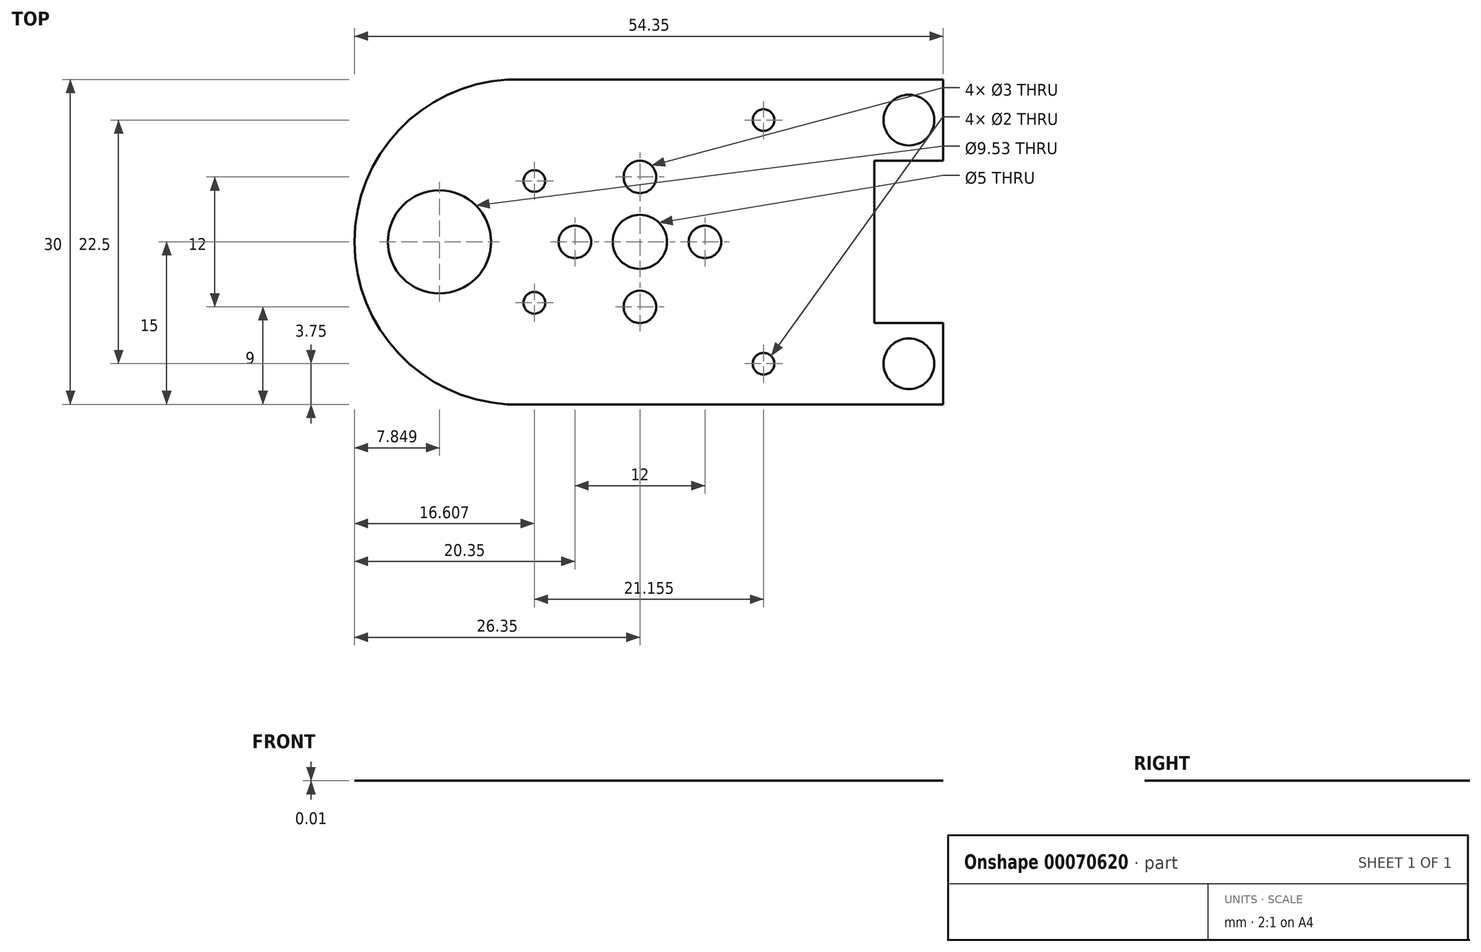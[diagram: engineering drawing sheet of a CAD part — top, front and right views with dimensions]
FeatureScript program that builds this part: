
annotation { "Feature Type Name" : "Feature", "Feature Type Description" : "" }
export const myFeature = defineFeature(function(context is Context, id is Id, definition is map)
    precondition{}
    {
        {
            var Q0;
            Q0=qCreatedBy(makeId("Top.planeOp"),FACE);
            var sketch = newSketch(context, id + "F0", { "sketchPlane" : qUnion([Q0])});
            skCircle(sketch, "E0.3.0", {"center": v(-6, 0) * mm, "radius": 1.5 * mm});
            skCircle(sketch, "E1", {"center": v(0, 0) * mm, "radius": 2.5 * mm});
            skCircle(sketch, "E0.1.0", {"center": v(-6, 0) * mm, "radius": 1.5 * mm});
            skLineSegment(sketch, "E2", {"start": v(-2.5, 0) * mm, "end": v(-9.5, 0) * mm});
            skLineSegment(sketch, "E3.bottom", {"start": v(-12.25, 15) * mm, "end": v(28, 15) * mm});
            skLineSegment(sketch, "E3.top", {"start": v(-12.25, -15) * mm, "end": v(28, -15) * mm});
            skLineSegment(sketch, "E3.right", {"start": v(28, 15) * mm, "end": v(28, -15) * mm});
            skCircle(sketch, "E4.1.0", {"center": v(0, -6) * mm, "radius": 1.5 * mm});
            skCircle(sketch, "E4.2.0", {"center": v(6, 0) * mm, "radius": 1.5 * mm});
            skCircle(sketch, "E4.3.0", {"center": v(0, 6) * mm, "radius": 1.5 * mm});
            skPoint(sketch, "E5", {"position": v(7.5, 0) * mm});
            skPoint(sketch, "E5.positionSnap0", {"position": v(10.05, 0) * mm});
            skLineSegment(sketch, "E6.bottom", {"start": v(21.65, 7.5) * mm, "end": v(28, 7.5) * mm});
            skLineSegment(sketch, "E6.top", {"start": v(21.65, -7.5) * mm, "end": v(28, -7.5) * mm});
            skLineSegment(sketch, "E6.left", {"start": v(21.65, 7.5) * mm, "end": v(21.65, -7.5) * mm});
            skLineSegment(sketch, "E6.right", {"start": v(28, 7.5) * mm, "end": v(28, -7.5) * mm});
            skPoint(sketch, "E7", {"position": v(24.83, 11.25) * mm});
            skPoint(sketch, "E8", {"position": v(24.83, -11.25) * mm});
            skPoint(sketch, "E9", {"position": v(0, 11.25) * mm});
            skPoint(sketch, "E10.1.0", {"position": v(-9.74, 5.63) * mm});
            skPoint(sketch, "E10.2.0", {"position": v(-9.74, -5.62) * mm});
            skPoint(sketch, "E10.3.0", {"position": v(0, -11.25) * mm});
            skPoint(sketch, "E10.4.0", {"position": v(9.74, -5.63) * mm});
            skPoint(sketch, "E10.5.0", {"position": v(9.74, 5.62) * mm});
            skLineSegment(sketch, "E11", {"start": v(-25.85, 3.84) * mm, "end": v(-25.85, -3.84) * mm});
            skPoint(sketch, "E12", {"position": v(-26.35, 0) * mm});
            skPoint(sketch, "E13", {"position": v(-25.85, 3.84) * mm});
            skPoint(sketch, "E14", {"position": v(-25.85, -3.84) * mm});
            skPoint(sketch, "E15", {"position": v(-12.25, 15) * mm});
            skPoint(sketch, "E16", {"position": v(-12.25, -15) * mm});
            skArc(sketch, "E17", {"start": v(-12.25, 15) * mm, "mid": v(-26.35, 0) * mm, "end": v(-12.25, -15) * mm});
            skCircle(sketch, "E18", {"center": v(-18.5, 0) * mm, "radius": 4.76 * mm});
            skSolve(sketch);
        }
        {
            var Q0;
            Q0=makeQuery(id+"F0.imprint","IMPRINT",FACE,{"disambiguationData":[TD([[makeQuery(id+"F0.imprint","IMPRINT",EDGE,{"derivedFrom":sQuery(id+"F0.wireOp",EDGE,"E1")}),-1.0]])]});
            var Q1;
            {var subQ2=sQuery(id+"F0.wireOp",EDGE,"E3.bottom");Q1=makeQuery(id+"F0.imprint","IMPRINT",FACE,{"disambiguationData":[TD([[makeQuery(id+"F0.imprint","IMPRINT",EDGE,{"derivedFrom":subQ2}),-1.0]])]});}
            extrude(context, id + "F1", {"entities" : qUnion([Q0, Q1]), "depth" : 1 / 101.6 * mm});
        }
        {
            var Q0;
            Q0=sQuery(id+"F0.wireOp",VERTEX,"E7");
            var Q1;
            Q1=sQuery(id+"F0.wireOp",VERTEX,"E8");
            var Q2;
            Q2=makeQuery(id+"F1.opExtrude","SWEPT_BODY",BODY,{"disambiguationData":[OSD([sQuery(id+"F0.wireOp",EDGE,"E1"),sQuery(id+"F0.wireOp",EDGE,"E0.1.0"),sQuery(id+"F0.wireOp",EDGE,"E3.bottom"),sQuery(id+"F0.wireOp",EDGE,"E3.top"),sQuery(id+"F0.wireOp",EDGE,"E3.right"),sQuery(id+"F0.wireOp",EDGE,"E4.1.0"),sQuery(id+"F0.wireOp",EDGE,"E4.2.0"),sQuery(id+"F0.wireOp",EDGE,"E4.3.0"),sQuery(id+"F0.wireOp",EDGE,"Qfz2i4fl-gXpp-EPbZ-7ioY-sWL0IBWqoAn5"),sQuery(id+"F0.wireOp",EDGE,"E6.bottom"),sQuery(id+"F0.wireOp",EDGE,"E6.top"),sQuery(id+"F0.wireOp",EDGE,"E6.left")])]});
            hole(context, id + "F2", {"style" : HoleStyle.C_SINK, "endStyle" : HoleEndStyle.THROUGH, "oppositeDirection" : true, "holeDiameter" : 2.5 * mm, "cSinkDiameter" : 4.7 * mm, "cSinkAngle" : 90 * degree, "locations" : qUnion([Q0, Q1]), "scope" : qUnion([Q2]), "isTappedThrough" : true});
        }
        {
            var Q0;
            Q0=makeQuery(id+"F1.opExtrude","SWEPT_FACE",FACE,{"disambiguationData":[OSD([sQuery(id+"F0.wireOp",EDGE,"E6.left")])]});
            var sketch = newSketch(context, id + "F3", { "sketchPlane" : qUnion([Q0])});
            skPoint(sketch, "E19", {"position": v(0, 3.18) * mm});
            skSolve(sketch);
        }
        {
            var Q0;
            Q0=sQuery(id+"F3.wireOp",VERTEX,"E19");
            var Q1;
            Q1=makeQuery(id+"F1.opExtrude","SWEPT_BODY",BODY,{"disambiguationData":[OSD([sQuery(id+"F0.wireOp",EDGE,"E1"),sQuery(id+"F0.wireOp",EDGE,"E0.1.0"),sQuery(id+"F0.wireOp",EDGE,"E3.bottom"),sQuery(id+"F0.wireOp",EDGE,"E3.top"),sQuery(id+"F0.wireOp",EDGE,"E3.right"),sQuery(id+"F0.wireOp",EDGE,"E4.1.0"),sQuery(id+"F0.wireOp",EDGE,"E4.2.0"),sQuery(id+"F0.wireOp",EDGE,"E4.3.0"),sQuery(id+"F0.wireOp",EDGE,"Qfz2i4fl-gXpp-EPbZ-7ioY-sWL0IBWqoAn5"),sQuery(id+"F0.wireOp",EDGE,"E6.bottom"),sQuery(id+"F0.wireOp",EDGE,"E6.top"),sQuery(id+"F0.wireOp",EDGE,"E6.left")])]});
            hole(context, id + "F4", {"style" : HoleStyle.SIMPLE, "endStyle" : HoleEndStyle.BLIND, "holeDiameter" : 2.05 * mm, "holeDepth" : 12.5 * mm, "locations" : qUnion([Q0]), "scope" : qUnion([Q1])});
        }
        {
            var Q0;
            Q0=sQuery(id+"F0.wireOp",VERTEX,"E10.2.0");
            var Q1;
            Q1=sQuery(id+"F0.wireOp",VERTEX,"E10.1.0");
            var Q2;
            Q2=makeQuery(id+"F1.opExtrude","SWEPT_BODY",BODY,{"disambiguationData":[OSD([sQuery(id+"F0.wireOp",EDGE,"E1"),sQuery(id+"F0.wireOp",EDGE,"E0.1.0"),sQuery(id+"F0.wireOp",EDGE,"E3.bottom"),sQuery(id+"F0.wireOp",EDGE,"E3.top"),sQuery(id+"F0.wireOp",EDGE,"E3.right"),sQuery(id+"F0.wireOp",EDGE,"E4.1.0"),sQuery(id+"F0.wireOp",EDGE,"E4.2.0"),sQuery(id+"F0.wireOp",EDGE,"E4.3.0"),sQuery(id+"F0.wireOp",EDGE,"Qfz2i4fl-gXpp-EPbZ-7ioY-sWL0IBWqoAn5"),sQuery(id+"F0.wireOp",EDGE,"E6.bottom"),sQuery(id+"F0.wireOp",EDGE,"E6.top"),sQuery(id+"F0.wireOp",EDGE,"E6.left")])]});
            hole(context, id + "F5", {"style" : HoleStyle.SIMPLE, "endStyle" : HoleEndStyle.BLIND, "oppositeDirection" : true, "holeDiameter" : 2 * mm, "holeDepth" : 8 * mm, "locations" : qUnion([Q0, Q1]), "scope" : qUnion([Q2])});
        }
        {
            var Q0;
            Q0=makeQuery(id+"F1.opExtrude","CAP_FACE",FACE,{"disambiguationData":[OSD([sQuery(id+"F0.wireOp",EDGE,"E1"),sQuery(id+"F0.wireOp",EDGE,"E0.1.0"),sQuery(id+"F0.wireOp",EDGE,"E3.bottom"),sQuery(id+"F0.wireOp",EDGE,"E3.top"),sQuery(id+"F0.wireOp",EDGE,"E3.right"),sQuery(id+"F0.wireOp",EDGE,"E4.1.0"),sQuery(id+"F0.wireOp",EDGE,"E4.2.0"),sQuery(id+"F0.wireOp",EDGE,"E4.3.0"),sQuery(id+"F0.wireOp",EDGE,"Qfz2i4fl-gXpp-EPbZ-7ioY-sWL0IBWqoAn5"),sQuery(id+"F0.wireOp",EDGE,"E6.bottom"),sQuery(id+"F0.wireOp",EDGE,"E6.top"),sQuery(id+"F0.wireOp",EDGE,"E6.left")])],"isStart":false});
            var sketch = newSketch(context, id + "F6", { "sketchPlane" : qUnion([Q0])});
            skPoint(sketch, "E20", {"position": v(11.41, 11.25) * mm});
            skPoint(sketch, "E21.MirrorP", {"position": v(11.41, -11.25) * mm});
            skSolve(sketch);
        }
        {
            var Q0;
            Q0=sQuery(id+"F6.wireOp",VERTEX,"E21.MirrorP");
            var Q1;
            Q1=sQuery(id+"F6.wireOp",VERTEX,"E20");
            var Q2;
            Q2=makeQuery(id+"F1.opExtrude","SWEPT_BODY",BODY,{"disambiguationData":[OSD([sQuery(id+"F0.wireOp",EDGE,"E1"),sQuery(id+"F0.wireOp",EDGE,"E0.1.0"),sQuery(id+"F0.wireOp",EDGE,"E3.bottom"),sQuery(id+"F0.wireOp",EDGE,"E3.top"),sQuery(id+"F0.wireOp",EDGE,"E3.right"),sQuery(id+"F0.wireOp",EDGE,"E4.1.0"),sQuery(id+"F0.wireOp",EDGE,"E4.2.0"),sQuery(id+"F0.wireOp",EDGE,"E4.3.0"),sQuery(id+"F0.wireOp",EDGE,"Qfz2i4fl-gXpp-EPbZ-7ioY-sWL0IBWqoAn5"),sQuery(id+"F0.wireOp",EDGE,"E6.bottom"),sQuery(id+"F0.wireOp",EDGE,"E6.top"),sQuery(id+"F0.wireOp",EDGE,"E6.left")])]});
            hole(context, id + "F7", {"style" : HoleStyle.SIMPLE, "endStyle" : HoleEndStyle.BLIND, "holeDiameter" : 2 * mm, "holeDepth" : 8 * mm, "locations" : qUnion([Q0, Q1]), "scope" : qUnion([Q2])});
        }
    });
